# Revit family: KEUCO_14953019000
name_source: partatom
category: Sonderausstattung
revit_build: Autodesk Revit 2016 (Build: 20150220_1215(x64)
units: mm (PartAtom-declared; Revit-internal decimal feet)

## family parameters
Arbeitsebenenbasiert = Nein
Beim Laden mit Abzugskörper schneiden = Nein
Bemaßung runder Anschluss = Durchmesser verwenden
Gemeinsam genutzt = Nein
Immer vertikal = Ja
Raumberechnungspunkt = Nein
Teiletyp = Normal

## types (3) — shared parameters
Beschreibung = Echtkristall mattiert, komplett mit Halter und Pumpe
Füllmenge: ca. 250 ml
Dosiermenge: ca. 0,5 ml/Hub
Gewicht = 382
Hersteller = KEUCO
Kategorie = ACC
Material Glas = Glas, weiß, hohe Luminanz
Preisgruppe = 1
Serie = Plan
URL = https://www.keuco.com
Verwendung = BI / GWC / WP

## per-type parameters (varying)
| type | Ausschreibungstext |
| 14953019000 | KEUCO PLAN Lotionspender 14953019000 
Hochglanzverchromter Lotionspender, Wandmodell 
komplett mit herausnehmbarem Echtkristalleinsatz 
für leichtes Reinigen und leichtes Befüllen
hochwertige und langlebige Pumpe
Füllmenge ca. 250 ml, für handelsübliche Flüssigseifen
Dosiermenge ca. 0,5 ml/Hub
Grundkörperdurchmesser 66 mm, Höhe 162 mm,Ausladung 123 mm
Der Lotionspender wird verdeckt angebracht
Lieferung inkl. korrosionsfreiem Befestigungsmaterial |
| 14953079000 | KEUCO PLAN Lotionspender 14953079000 
Lotionspender aus hochwertigem Edelstahl, Wandmodell
komplett mit herausnehmbarem Echtkristalleinsatz 
für leichtes Reinigen und leichtes Befüllen
hochwertige und langlebige Pumpe
Füllmenge ca. 250 ml, für handelsübliche Flüssigseifen
Dosiermenge ca. 0,5 ml/Hub
Grundkörperdurchmesser 66 mm, Höhe 162 mm, Ausladung 123 mm
Der Lotionspender wird verdeckt angebracht
Lieferung inkl. korrosionsfreiem Befestigungsmaterial |
| 14953179000 | KEUCO PLAN Lotionspender 14953179000 
Lotionspender Aluminium silber-eloxiert (E6 EV1)/verchromt 
Wandmodell, komplett mit herausnehmbarem Echtkristalleinsatz 
für leichtes Reinigen und leichtes Befüllen
hochwertige und langlebige Pumpe
Füllmenge ca. 250 ml, für handelsübliche Flüssigseifen
Dosiermenge ca. 0,5 ml/Hub
Grundkörperdurchmesser 66 mm, Höhe 162 mm, Ausladung 123 mm
Der Lotionspender verdeckt angebracht
Lieferung inkl. korrosionsfreiem Befestigungsmaterial |

note: column(s) folded — value = type name in every type: Artikelnummer

## geometry (parser evidence)
native form markers: Blend x4, Sweep x2
no freeform markers — native parametric forms only
